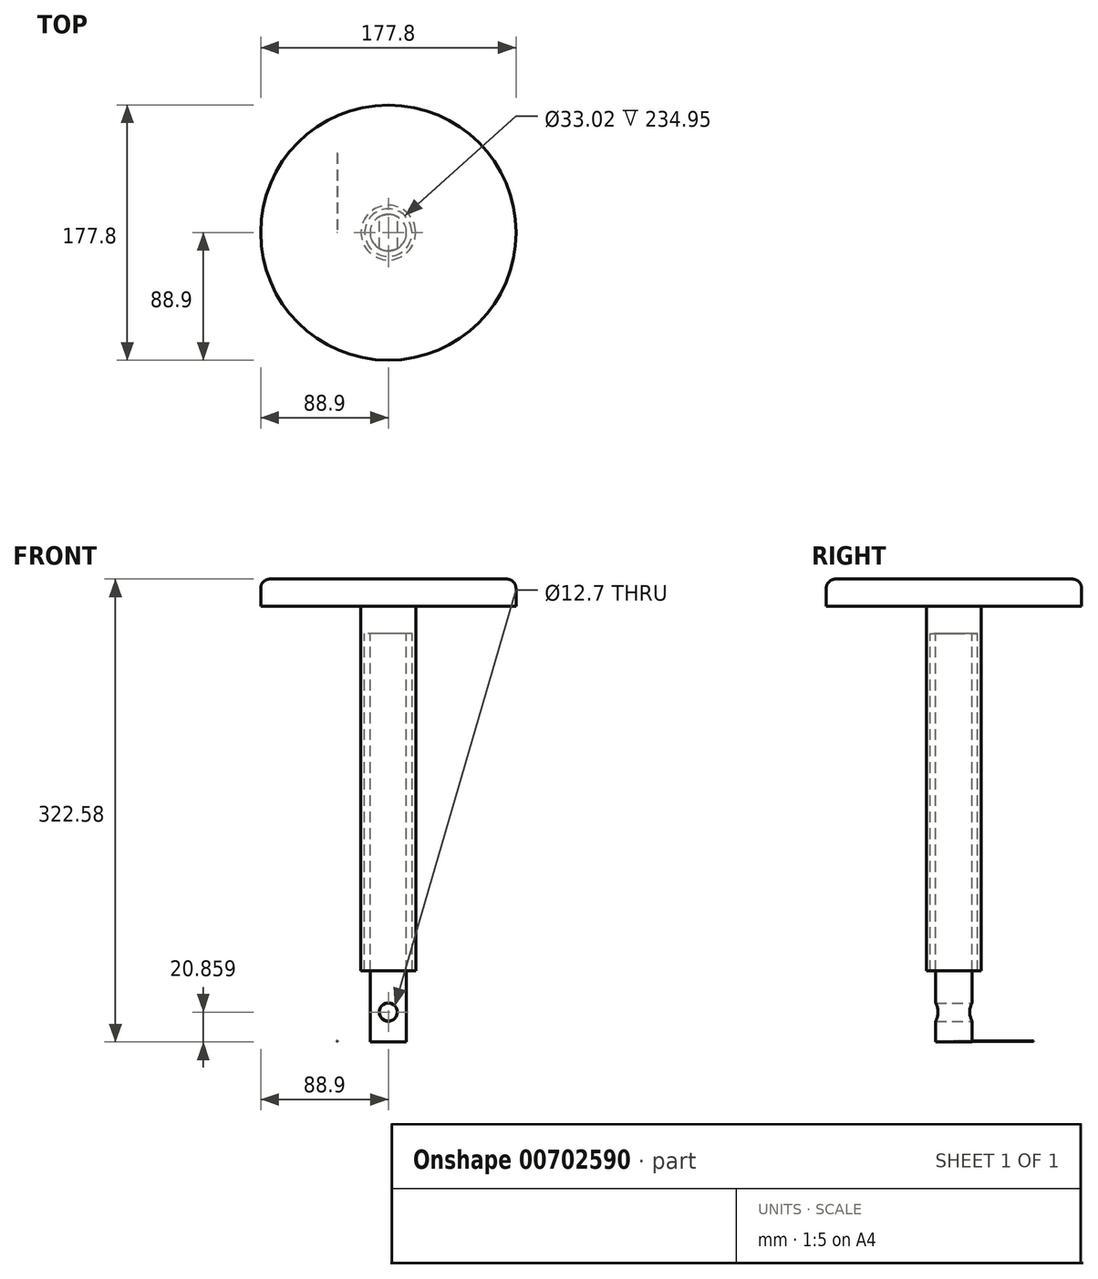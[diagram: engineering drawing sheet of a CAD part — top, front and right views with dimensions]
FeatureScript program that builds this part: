
annotation { "Feature Type Name" : "Feature", "Feature Type Description" : "" }
export const myFeature = defineFeature(function(context is Context, id is Id, definition is map)
    precondition{}
    {
        {
            var Q0;
            Q0=qCreatedBy(makeId("Top.planeOp"),FACE);
            var sketch = newSketch(context, id + "F0", { "sketchPlane" : qUnion([Q0])});
            skCircle(sketch, "E0", {"center": v(0, 0) * mm, "radius": 88.9 * mm});
            skCircle(sketch, "E1", {"center": v(0, 0) * mm, "radius": 19.05 * mm});
            skCircle(sketch, "E2", {"center": v(0, 0) * mm, "radius": 16.51 * mm});
            skSolve(sketch);
        }
        {
            var Q0;
            Q0=makeQuery(id+"F0.imprint","IMPRINT",FACE,{"disambiguationData":[TD([[makeQuery(id+"F0.imprint","IMPRINT",EDGE,{"derivedFrom":sQuery(id+"F0.wireOp",EDGE,"E0")}),1.0]])]});
            extrude(context, id + "F1", {"entities" : qUnion([Q0]), "depth" : 19.05 * mm, "offsetDistance" : 25.4 * mm});
        }
        {
            var Q0;
            Q0=makeQuery(id+"F0.imprint","IMPRINT",FACE,{"disambiguationData":[TD([[makeQuery(id+"F0.imprint","IMPRINT",EDGE,{"derivedFrom":sQuery(id+"F0.wireOp",EDGE,"E1")}),1.0]])]});
            extrude(context, id + "F2", {"entities" : qUnion([Q0]), "operationType" : NewBodyOperationType.ADD, "oppositeDirection" : true, "depth" : 254 * mm, "offsetDistance" : 25.4 * mm, "hasSecondDirection" : true, "secondDirectionOppositeDirection" : false, "secondDirectionDepth" : 19.05 * mm});
        }
        {
            var Q0;
            Q0=makeQuery(id+"F1.opExtrude","CAP_EDGE",EDGE,{"disambiguationData":[OSD([sQuery(id+"F0.wireOp",EDGE,"E0")])],"isStart":false});
            fillet(context, id + "F3", {"entities" : qUnion([Q0]), "radius" : 6.35 * mm, "tangentPropagation" : true, "allowEdgeOverflow" : false});
        }
        {
            var Q0;
            Q0=makeQuery(id+"F0.imprint","IMPRINT",FACE,{"disambiguationData":[TD([[makeQuery(id+"F0.imprint","IMPRINT",EDGE,{"derivedFrom":sQuery(id+"F0.wireOp",EDGE,"E2")}),1.0]])]});
            extrude(context, id + "F4", {"entities" : qUnion([Q0]), "operationType" : NewBodyOperationType.ADD, "depth" : 19.05 * mm, "offsetDistance" : 25.4 * mm, "hasSecondDirection" : true, "secondDirectionOppositeDirection" : true, "secondDirectionDepth" : 19.05 * mm});
        }
        {
            var Q0;
            Q0=makeQuery(id+"F4.opExtrude","CAP_FACE",FACE,{"disambiguationData":[OSD([sQuery(id+"F0.wireOp",EDGE,"E2")])],"isStart":true});
            var sketch = newSketch(context, id + "F5", { "sketchPlane" : qUnion([Q0])});
            skCircle(sketch, "E3", {"center": v(0, 0) * mm, "radius": 12.7 * mm});
            skSolve(sketch);
        }
        {
            var Q0;
            Q0=makeQuery(id+"F5.imprint","IMPRINT",FACE,{"disambiguationData":[TD([[makeQuery(id+"F5.imprint","IMPRINT",EDGE,{"derivedFrom":sQuery(id+"F5.wireOp",EDGE,"E3")}),1.0]])]});
            extrude(context, id + "F6", {"entities" : qUnion([Q0]), "operationType" : NewBodyOperationType.ADD, "depth" : 284.48 * mm, "offsetDistance" : 25.4 * mm});
        }
        {
            var Q0;
            Q0=qCreatedBy(makeId("Front.planeOp"),FACE);
            var sketch = newSketch(context, id + "F7", { "sketchPlane" : qUnion([Q0])});
            skLineSegment(sketch, "E4.bottom", {"start": v(-35.42, -302.77) * mm, "end": v(-35.67, -302.77) * mm});
            skLineSegment(sketch, "E4.top", {"start": v(-35.42, -303.02) * mm, "end": v(-35.67, -303.02) * mm});
            skLineSegment(sketch, "E4.left", {"start": v(-35.42, -302.77) * mm, "end": v(-35.42, -303.02) * mm});
            skLineSegment(sketch, "E4.right", {"start": v(-35.67, -302.77) * mm, "end": v(-35.67, -303.02) * mm});
            skSolve(sketch);
        }
        {
            var Q0;
            Q0 = qSketchRegion(id + "F7", true);
            extrude(context, id + "F8", {"entities" : qUnion([Q0]), "operationType" : NewBodyOperationType.ADD, "oppositeDirection" : true, "depth" : 55.37 * mm, "offsetDistance" : 25.4 * mm});
        }
        {
            var Q0;
            Q0=makeQuery(id+"F8.opExtrude","CAP_FACE",FACE,{"disambiguationData":[OSD([sQuery(id+"F7.wireOp",EDGE,"E4.bottom"),sQuery(id+"F7.wireOp",EDGE,"E4.top"),sQuery(id+"F7.wireOp",EDGE,"E4.left"),sQuery(id+"F7.wireOp",EDGE,"E4.right")])],"isStart":false});
            var sketch = newSketch(context, id + "F9", { "sketchPlane" : qUnion([Q0])});
            skCircle(sketch, "E5", {"center": v(0, -282.67) * mm, "radius": 6.35 * mm});
            skSolve(sketch);
        }
        {
            var Q0;
            Q0=makeQuery(id+"F9.imprint","IMPRINT",FACE,{"disambiguationData":[TD([[makeQuery(id+"F9.imprint","IMPRINT",EDGE,{"derivedFrom":sQuery(id+"F9.wireOp",EDGE,"E5")}),1.0]])]});
            extrude(context, id + "F10", {"entities" : qUnion([Q0]), "operationType" : NewBodyOperationType.REMOVE, "endBound" : BoundingType.THROUGH_ALL, "oppositeDirection" : true, "depth" : 25.4 * mm, "offsetDistance" : 25.4 * mm});
        }
    });
